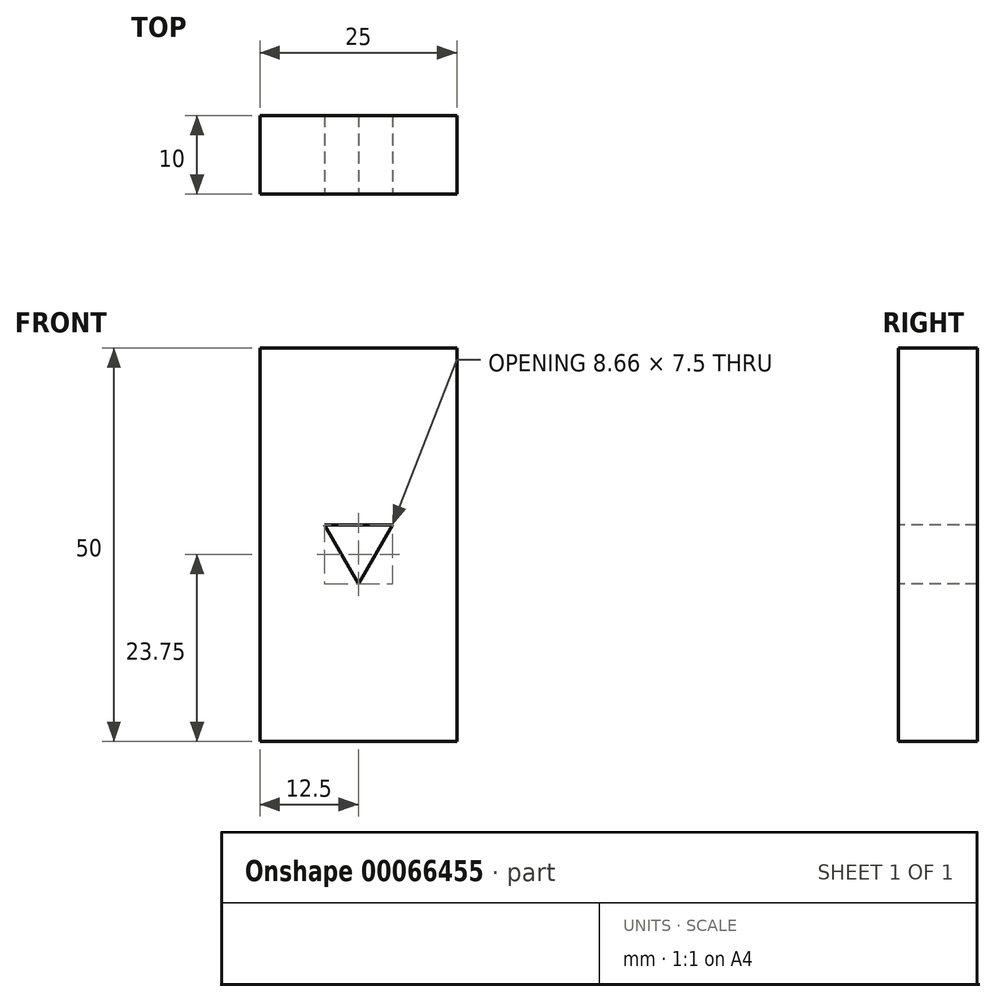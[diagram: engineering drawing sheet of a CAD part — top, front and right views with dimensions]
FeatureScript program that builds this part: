
annotation { "Feature Type Name" : "Feature", "Feature Type Description" : "" }
export const myFeature = defineFeature(function(context is Context, id is Id, definition is map)
    precondition{}
    {
        {
            var Q0;
            Q0=qCreatedBy(makeId("Front.planeOp"),FACE);
            var sketch = newSketch(context, id + "F0", { "sketchPlane" : qUnion([Q0])});
            skLineSegment(sketch, "E0.rect.bottom", {"start": v(12.5, 25) * mm, "end": v(-12.5, 25) * mm});
            skLineSegment(sketch, "E0.rect.top", {"start": v(12.5, -25) * mm, "end": v(-12.5, -25) * mm});
            skLineSegment(sketch, "E0.rect.left", {"start": v(12.5, 25) * mm, "end": v(12.5, -25) * mm});
            skLineSegment(sketch, "E0.rect.right", {"start": v(-12.5, 25) * mm, "end": v(-12.5, -25) * mm});
            skPoint(sketch, "E0.rect.middle", {"position": v(0, 0) * mm});
            skSolve(sketch);
        }
        {
            var Q0;
            Q0 = qSketchRegion(id + "F0", true);
            extrude(context, id + "F1", {"entities" : qUnion([Q0]), "endBound" : BoundingType.SYMMETRIC, "depth" : 10 * mm});
        }
        {
            var Q0;
            Q0=makeQuery(id+"F1.opExtrude","CAP_FACE",FACE,{"disambiguationData":[OSD([sQuery(id+"F0.wireOp",EDGE,"E0.rect.bottom"),sQuery(id+"F0.wireOp",EDGE,"E0.rect.top"),sQuery(id+"F0.wireOp",EDGE,"E0.rect.left"),sQuery(id+"F0.wireOp",EDGE,"E0.rect.right")])],"isStart":false});
            var sketch = newSketch(context, id + "F2", { "sketchPlane" : qUnion([Q0])});
            skCircle(sketch, "E1.cCircle", {"center": v(0, 0) * mm, "radius": 2.5 * mm, "construction": true});
            skLineSegment(sketch, "E1.0", {"start": v(-4.33, 2.5) * mm, "end": v(4.33, 2.5) * mm});
            skLineSegment(sketch, "E1.1", {"start": v(4.33, 2.5) * mm, "end": v(0, -5) * mm});
            skLineSegment(sketch, "E1.2", {"start": v(0, -5) * mm, "end": v(-4.33, 2.5) * mm});
            skPoint(sketch, "E1.0.midPoint", {"position": v(0, 2.5) * mm});
            skSolve(sketch);
        }
        {
            var Q0;
            Q0 = qSketchRegion(id + "F2", true);
            extrude(context, id + "F3", {"entities" : qUnion([Q0]), "operationType" : NewBodyOperationType.REMOVE, "endBound" : BoundingType.THROUGH_ALL, "oppositeDirection" : true, "depth" : 25 * mm});
        }
    });
